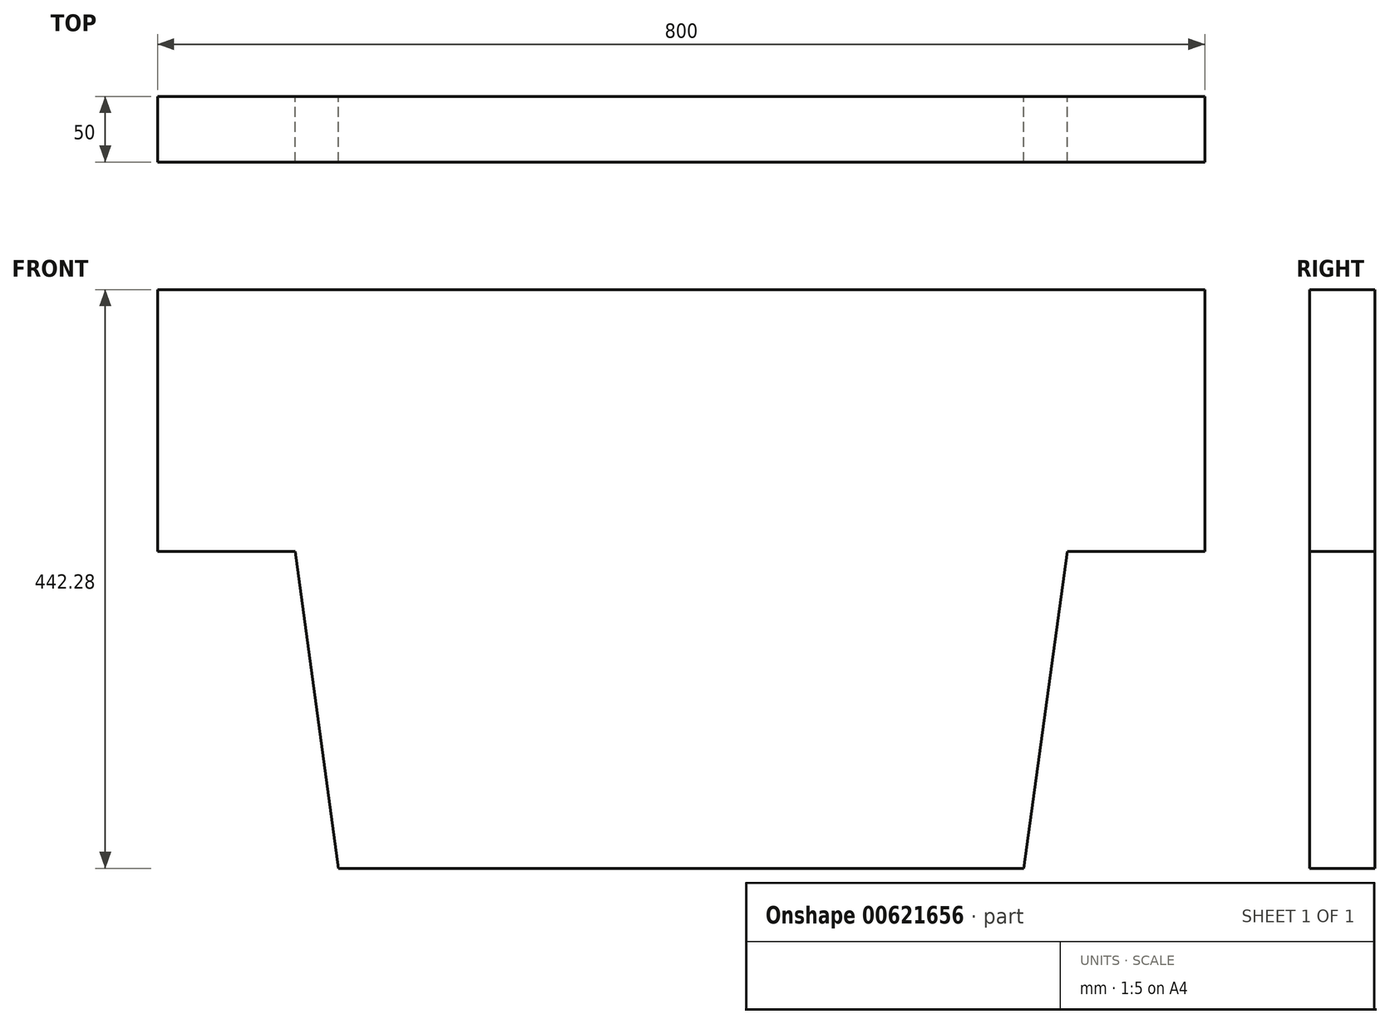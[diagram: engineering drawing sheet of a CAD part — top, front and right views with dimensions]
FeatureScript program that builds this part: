
annotation { "Feature Type Name" : "Feature", "Feature Type Description" : "" }
export const myFeature = defineFeature(function(context is Context, id is Id, definition is map)
    precondition{}
    {
        {
            var Q0;
            Q0=qCreatedBy(makeId("Front.planeOp"),FACE);
            var sketch = newSketch(context, id + "F0", { "sketchPlane" : qUnion([Q0])});
            skLineSegment(sketch, "E0", {"start": v(0, 0) * mm, "end": v(-6.84, 50) * mm, "construction": true});
            skLineSegment(sketch, "E1", {"start": v(-40, 292.28) * mm, "end": v(-145, 292.28) * mm});
            skLineSegment(sketch, "E2", {"start": v(-145, 292.28) * mm, "end": v(-145, 492.28) * mm});
            skLineSegment(sketch, "E3", {"start": v(-145, 492.28) * mm, "end": v(655, 492.28) * mm});
            skLineSegment(sketch, "E4", {"start": v(655, 492.28) * mm, "end": v(655, 292.28) * mm});
            skLineSegment(sketch, "E5", {"start": v(655, 292.28) * mm, "end": v(550, 292.28) * mm});
            skLineSegment(sketch, "E6", {"start": v(550, 292.28) * mm, "end": v(516.84, 50) * mm});
            skLineSegment(sketch, "E7", {"start": v(510, 0) * mm, "end": v(0, 0) * mm, "construction": true});
            skLineSegment(sketch, "E8", {"start": v(255, 492.28) * mm, "end": v(255, 0) * mm, "construction": true});
            skLineSegment(sketch, "E9", {"start": v(-6.84, 50) * mm, "end": v(516.84, 50) * mm});
            skLineSegment(sketch, "E10", {"start": v(-6.84, 50) * mm, "end": v(-40, 292.28) * mm});
            skLineSegment(sketch, "E11", {"start": v(516.84, 50) * mm, "end": v(510, 0) * mm, "construction": true});
            skSolve(sketch);
        }
        {
            var Q0;
            Q0 = qSketchRegion(id + "F0", true);
            extrude(context, id + "F1", {"entities" : qUnion([Q0]), "depth" : 50 * mm, "offsetDistance" : 25 * mm});
        }
    });
